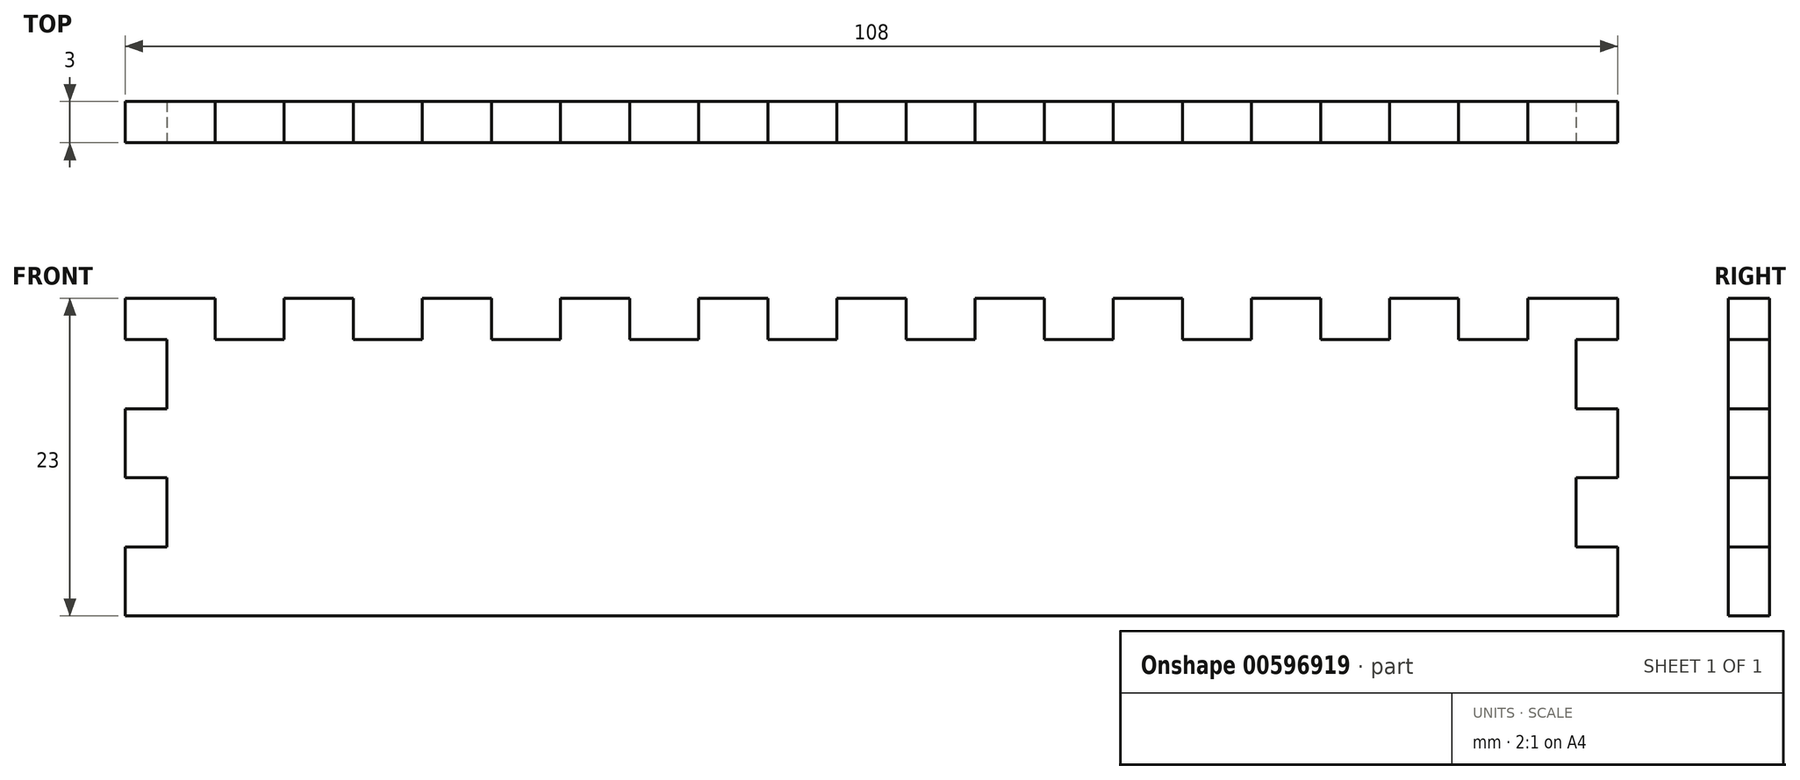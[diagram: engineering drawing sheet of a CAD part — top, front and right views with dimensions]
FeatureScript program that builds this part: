
annotation { "Feature Type Name" : "Feature", "Feature Type Description" : "" }
export const myFeature = defineFeature(function(context is Context, id is Id, definition is map)
    precondition{}
    {
        {
            var Q0;
            Q0=qCreatedBy(makeId("Front.planeOp"),FACE);
            var sketch = newSketch(context, id + "F0", { "sketchPlane" : qUnion([Q0])});
            skLineSegment(sketch, "E0.bottom", {"start": v(51, 20) * mm, "end": v(-51, 20) * mm});
            skLineSegment(sketch, "E0.top", {"start": v(51, -20) * mm, "end": v(-51, -20) * mm});
            skLineSegment(sketch, "E0.left", {"start": v(51, 20) * mm, "end": v(51, -20) * mm});
            skLineSegment(sketch, "E0.right", {"start": v(-51, 20) * mm, "end": v(-51, -20) * mm});
            skPoint(sketch, "E0.middle", {"position": v(0, 0) * mm});
            skSolve(sketch);
        }
        {
            var Q0;
            Q0=qSketchRegion(id+"F0",true);
            extrude(context, id + "F1", {"entities" : qUnion([Q0]), "depth" : 3 * mm, "offsetDistance" : 25 * mm});
        }
        {
            var Q0;
            Q0=makeQuery(id+"F1.opExtrude","CAP_FACE",FACE,{"disambiguationData":[OSD([sQuery(id+"F0.wireOp",EDGE,"E0.bottom"),sQuery(id+"F0.wireOp",EDGE,"E0.top"),sQuery(id+"F0.wireOp",EDGE,"E0.left"),sQuery(id+"F0.wireOp",EDGE,"E0.right")])],"isStart":false});
            var sketch = newSketch(context, id + "F2", { "sketchPlane" : qUnion([Q0])});
            skLineSegment(sketch, "E1.bottom", {"start": v(-51, -20) * mm, "end": v(-54, -20) * mm});
            skLineSegment(sketch, "E1.top", {"start": v(-51, -15) * mm, "end": v(-54, -15) * mm});
            skLineSegment(sketch, "E1.left", {"start": v(-51, -20) * mm, "end": v(-51, -15) * mm});
            skLineSegment(sketch, "E1.right", {"start": v(-54, -20) * mm, "end": v(-54, -15) * mm});
            skLineSegment(sketch, "E2.0.1.0", {"start": v(-51, -5) * mm, "end": v(-54, -5) * mm});
            skLineSegment(sketch, "E2.0.1.1", {"start": v(-54, -10) * mm, "end": v(-54, -5) * mm});
            skLineSegment(sketch, "E2.0.1.2", {"start": v(-51, -10) * mm, "end": v(-51, -5) * mm});
            skLineSegment(sketch, "E2.0.1.3", {"start": v(-51, -10) * mm, "end": v(-54, -10) * mm});
            skLineSegment(sketch, "E2.0.2.0", {"start": v(-51, 5) * mm, "end": v(-54, 5) * mm});
            skLineSegment(sketch, "E2.0.2.1", {"start": v(-54, 0) * mm, "end": v(-54, 5) * mm});
            skLineSegment(sketch, "E2.0.2.2", {"start": v(-51, 0) * mm, "end": v(-51, 5) * mm});
            skLineSegment(sketch, "E2.0.2.3", {"start": v(-51, 0) * mm, "end": v(-54, 0) * mm});
            skLineSegment(sketch, "E2.0.3.0", {"start": v(-51, 15) * mm, "end": v(-54, 15) * mm});
            skLineSegment(sketch, "E2.0.3.1", {"start": v(-54, 10) * mm, "end": v(-54, 15) * mm});
            skLineSegment(sketch, "E2.0.3.2", {"start": v(-51, 10) * mm, "end": v(-51, 15) * mm});
            skLineSegment(sketch, "E2.0.3.3", {"start": v(-51, 10) * mm, "end": v(-54, 10) * mm});
            skLineSegment(sketch, "E2.direction1", {"start": v(-54, -15) * mm, "end": v(-29, -15) * mm, "construction": true});
            skLineSegment(sketch, "E2.direction2", {"start": v(-54, -15) * mm, "end": v(-54, -5) * mm, "construction": true});
            skLineSegment(sketch, "E3.MirrorCS", {"start": v(54, -10) * mm, "end": v(54, -5) * mm});
            skLineSegment(sketch, "E4.MirrorCS", {"start": v(51, -5) * mm, "end": v(54, -5) * mm});
            skLineSegment(sketch, "E5.MirrorCS", {"start": v(51, -20) * mm, "end": v(51, -15) * mm});
            skLineSegment(sketch, "E6.MirrorCS", {"start": v(54, 10) * mm, "end": v(54, 15) * mm});
            skLineSegment(sketch, "E7.MirrorCS", {"start": v(51, -20) * mm, "end": v(54, -20) * mm});
            skLineSegment(sketch, "E8.MirrorCS", {"start": v(51, -15) * mm, "end": v(54, -15) * mm});
            skLineSegment(sketch, "E9.MirrorCS", {"start": v(54, -20) * mm, "end": v(54, -15) * mm});
            skLineSegment(sketch, "E10.MirrorCS", {"start": v(51, 15) * mm, "end": v(54, 15) * mm});
            skLineSegment(sketch, "E11.MirrorCS", {"start": v(51, 10) * mm, "end": v(54, 10) * mm});
            skLineSegment(sketch, "E12.MirrorCS", {"start": v(54, -15) * mm, "end": v(54, -5) * mm, "construction": true});
            skLineSegment(sketch, "E13.MirrorCS", {"start": v(51, 10) * mm, "end": v(51, 15) * mm});
            skLineSegment(sketch, "E14.MirrorCS", {"start": v(54, 0) * mm, "end": v(54, 5) * mm});
            skLineSegment(sketch, "E15.MirrorCS", {"start": v(51, 0) * mm, "end": v(51, 5) * mm});
            skLineSegment(sketch, "E16.MirrorCS", {"start": v(51, 0) * mm, "end": v(54, 0) * mm});
            skLineSegment(sketch, "E17.MirrorCS", {"start": v(51, -10) * mm, "end": v(51, -5) * mm});
            skLineSegment(sketch, "E18.MirrorCS", {"start": v(51, -10) * mm, "end": v(54, -10) * mm});
            skLineSegment(sketch, "E19.MirrorCS", {"start": v(51, 5) * mm, "end": v(54, 5) * mm});
            skSolve(sketch);
        }
        {
            var Q0;
            Q0=qSketchRegion(id+"F2",true);
            extrude(context, id + "F3", {"entities" : qUnion([Q0]), "operationType" : NewBodyOperationType.ADD, "oppositeDirection" : true, "depth" : 3 * mm, "offsetDistance" : 25 * mm});
        }
        {
            var Q0;
            Q0=makeQuery(id+"F3.boolean.opBoolean","MERGE",FACE,{"derivedFrom":[makeQuery(id+"F1.opExtrude","CAP_FACE",FACE,{"disambiguationData":[OSD([sQuery(id+"F0.wireOp",EDGE,"E0.bottom"),sQuery(id+"F0.wireOp",EDGE,"E0.top"),sQuery(id+"F0.wireOp",EDGE,"E0.left"),sQuery(id+"F0.wireOp",EDGE,"E0.right")])],"isStart":true}),makeQuery(id+"F3.opExtrude","CAP_FACE",FACE,{"disambiguationData":[OSD([sQuery(id+"F2.wireOp",EDGE,"E1.bottom"),sQuery(id+"F2.wireOp",EDGE,"E1.top"),sQuery(id+"F2.wireOp",EDGE,"E1.left"),sQuery(id+"F2.wireOp",EDGE,"E1.right")])],"isStart":false}),makeQuery(id+"F3.opExtrude","CAP_FACE",FACE,{"disambiguationData":[OSD([sQuery(id+"F2.wireOp",EDGE,"E2.0.1.0"),sQuery(id+"F2.wireOp",EDGE,"E2.0.1.1"),sQuery(id+"F2.wireOp",EDGE,"E2.0.1.2"),sQuery(id+"F2.wireOp",EDGE,"E2.0.1.3")])],"isStart":false}),makeQuery(id+"F3.opExtrude","CAP_FACE",FACE,{"disambiguationData":[OSD([sQuery(id+"F2.wireOp",EDGE,"E2.0.2.0"),sQuery(id+"F2.wireOp",EDGE,"E2.0.2.1"),sQuery(id+"F2.wireOp",EDGE,"E2.0.2.2"),sQuery(id+"F2.wireOp",EDGE,"E2.0.2.3")])],"isStart":false}),makeQuery(id+"F3.opExtrude","CAP_FACE",FACE,{"disambiguationData":[OSD([sQuery(id+"F2.wireOp",EDGE,"E2.0.3.0"),sQuery(id+"F2.wireOp",EDGE,"E2.0.3.1"),sQuery(id+"F2.wireOp",EDGE,"E2.0.3.2"),sQuery(id+"F2.wireOp",EDGE,"E2.0.3.3")])],"isStart":false}),makeQuery(id+"F3.opExtrude","CAP_FACE",FACE,{"disambiguationData":[OSD([sQuery(id+"F2.wireOp",EDGE,"E3.MirrorCS"),sQuery(id+"F2.wireOp",EDGE,"E4.MirrorCS"),sQuery(id+"F2.wireOp",EDGE,"E17.MirrorCS"),sQuery(id+"F2.wireOp",EDGE,"E18.MirrorCS")])],"isStart":false}),makeQuery(id+"F3.opExtrude","CAP_FACE",FACE,{"disambiguationData":[OSD([sQuery(id+"F2.wireOp",EDGE,"E5.MirrorCS"),sQuery(id+"F2.wireOp",EDGE,"E7.MirrorCS"),sQuery(id+"F2.wireOp",EDGE,"E8.MirrorCS"),sQuery(id+"F2.wireOp",EDGE,"E9.MirrorCS")])],"isStart":false}),makeQuery(id+"F3.opExtrude","CAP_FACE",FACE,{"disambiguationData":[OSD([sQuery(id+"F2.wireOp",EDGE,"E6.MirrorCS"),sQuery(id+"F2.wireOp",EDGE,"E10.MirrorCS"),sQuery(id+"F2.wireOp",EDGE,"E11.MirrorCS"),sQuery(id+"F2.wireOp",EDGE,"E13.MirrorCS")])],"isStart":false}),makeQuery(id+"F3.opExtrude","CAP_FACE",FACE,{"disambiguationData":[OSD([sQuery(id+"F2.wireOp",EDGE,"E14.MirrorCS"),sQuery(id+"F2.wireOp",EDGE,"E15.MirrorCS"),sQuery(id+"F2.wireOp",EDGE,"E16.MirrorCS"),sQuery(id+"F2.wireOp",EDGE,"E19.MirrorCS")])],"isStart":false})]});
            var sketch = newSketch(context, id + "F4", { "sketchPlane" : qUnion([Q0])});
            skLineSegment(sketch, "E20", {"start": v(0, 20) * mm, "end": v(0, 21.5) * mm, "construction": true});
            skLineSegment(sketch, "E21.bottom", {"start": v(-2.5, 20) * mm, "end": v(2.5, 20) * mm});
            skLineSegment(sketch, "E21.top", {"start": v(-2.5, 23) * mm, "end": v(2.5, 23) * mm});
            skLineSegment(sketch, "E21.left", {"start": v(-2.5, 20) * mm, "end": v(-2.5, 23) * mm});
            skLineSegment(sketch, "E21.right", {"start": v(2.5, 20) * mm, "end": v(2.5, 23) * mm});
            skPoint(sketch, "E21.middle", {"position": v(0, 21.5) * mm});
            skLineSegment(sketch, "E22.1.0.0", {"start": v(7.5, 23) * mm, "end": v(12.5, 23) * mm});
            skLineSegment(sketch, "E22.1.0.1", {"start": v(12.5, 20) * mm, "end": v(12.5, 23) * mm});
            skLineSegment(sketch, "E22.1.0.2", {"start": v(7.5, 20) * mm, "end": v(12.5, 20) * mm});
            skLineSegment(sketch, "E22.1.0.3", {"start": v(7.5, 20) * mm, "end": v(7.5, 23) * mm});
            skLineSegment(sketch, "E22.2.0.0", {"start": v(17.5, 23) * mm, "end": v(22.5, 23) * mm});
            skLineSegment(sketch, "E22.2.0.1", {"start": v(22.5, 20) * mm, "end": v(22.5, 23) * mm});
            skLineSegment(sketch, "E22.2.0.2", {"start": v(17.5, 20) * mm, "end": v(22.5, 20) * mm});
            skLineSegment(sketch, "E22.2.0.3", {"start": v(17.5, 20) * mm, "end": v(17.5, 23) * mm});
            skLineSegment(sketch, "E22.3.0.0", {"start": v(27.5, 23) * mm, "end": v(32.5, 23) * mm});
            skLineSegment(sketch, "E22.3.0.1", {"start": v(32.5, 20) * mm, "end": v(32.5, 23) * mm});
            skLineSegment(sketch, "E22.3.0.2", {"start": v(27.5, 20) * mm, "end": v(32.5, 20) * mm});
            skLineSegment(sketch, "E22.3.0.3", {"start": v(27.5, 20) * mm, "end": v(27.5, 23) * mm});
            skLineSegment(sketch, "E22.4.0.0", {"start": v(37.5, 23) * mm, "end": v(42.5, 23) * mm});
            skLineSegment(sketch, "E22.4.0.1", {"start": v(42.5, 20) * mm, "end": v(42.5, 23) * mm});
            skLineSegment(sketch, "E22.4.0.2", {"start": v(37.5, 20) * mm, "end": v(42.5, 20) * mm});
            skLineSegment(sketch, "E22.4.0.3", {"start": v(37.5, 20) * mm, "end": v(37.5, 23) * mm});
            skLineSegment(sketch, "E22.5.0.0", {"start": v(47.5, 23) * mm, "end": v(52.5, 23) * mm});
            skLineSegment(sketch, "E22.5.0.2", {"start": v(47.5, 20) * mm, "end": v(52.5, 20) * mm});
            skLineSegment(sketch, "E22.5.0.3", {"start": v(47.5, 20) * mm, "end": v(47.5, 23) * mm});
            skLineSegment(sketch, "E22.direction1", {"start": v(-2.5, 23) * mm, "end": v(7.5, 23) * mm, "construction": true});
            skLineSegment(sketch, "E23.MirrorCS", {"start": v(-47.5, 20) * mm, "end": v(-47.5, 23) * mm});
            skLineSegment(sketch, "E24.MirrorCS", {"start": v(-17.5, 20) * mm, "end": v(-17.5, 23) * mm});
            skLineSegment(sketch, "E25.MirrorCS", {"start": v(-22.5, 20) * mm, "end": v(-22.5, 23) * mm});
            skLineSegment(sketch, "E26.MirrorCS", {"start": v(-7.5, 20) * mm, "end": v(-7.5, 23) * mm});
            skLineSegment(sketch, "E27.MirrorCS", {"start": v(-12.5, 20) * mm, "end": v(-12.5, 23) * mm});
            skLineSegment(sketch, "E28.MirrorCS", {"start": v(-32.5, 20) * mm, "end": v(-32.5, 23) * mm});
            skLineSegment(sketch, "E29.MirrorCS", {"start": v(-37.5, 20) * mm, "end": v(-37.5, 23) * mm});
            skLineSegment(sketch, "E30.MirrorCS", {"start": v(-27.5, 20) * mm, "end": v(-27.5, 23) * mm});
            skLineSegment(sketch, "E31.MirrorCS", {"start": v(-42.5, 20) * mm, "end": v(-42.5, 23) * mm});
            skLineSegment(sketch, "E32.MirrorCS", {"start": v(-37.5, 23) * mm, "end": v(-42.5, 23) * mm});
            skLineSegment(sketch, "E33.MirrorCS", {"start": v(-47.5, 23) * mm, "end": v(-52.5, 23) * mm});
            skLineSegment(sketch, "E34.MirrorCS", {"start": v(-17.5, 20) * mm, "end": v(-22.5, 20) * mm});
            skLineSegment(sketch, "E35.MirrorCS", {"start": v(-17.5, 23) * mm, "end": v(-22.5, 23) * mm});
            skLineSegment(sketch, "E36.MirrorCS", {"start": v(-7.5, 20) * mm, "end": v(-12.5, 20) * mm});
            skLineSegment(sketch, "E37.MirrorCS", {"start": v(-7.5, 23) * mm, "end": v(-12.5, 23) * mm});
            skLineSegment(sketch, "E38.MirrorCS", {"start": v(-47.5, 20) * mm, "end": v(-52.5, 20) * mm});
            skLineSegment(sketch, "E39.MirrorCS", {"start": v(-27.5, 20) * mm, "end": v(-32.5, 20) * mm});
            skLineSegment(sketch, "E40.MirrorCS", {"start": v(-27.5, 23) * mm, "end": v(-32.5, 23) * mm});
            skLineSegment(sketch, "E41.MirrorCS", {"start": v(-37.5, 20) * mm, "end": v(-42.5, 20) * mm});
            skLineSegment(sketch, "E42", {"start": v(-52.5, 20) * mm, "end": v(-54, 20) * mm});
            skLineSegment(sketch, "E43", {"start": v(-54, 20) * mm, "end": v(-54, 23) * mm});
            skLineSegment(sketch, "E44", {"start": v(-54, 23) * mm, "end": v(-52.5, 23) * mm});
            skLineSegment(sketch, "E45.bottom", {"start": v(52.5, 23) * mm, "end": v(54, 23) * mm});
            skLineSegment(sketch, "E45.top", {"start": v(52.5, 20) * mm, "end": v(54, 20) * mm});
            skLineSegment(sketch, "E45.right", {"start": v(54, 23) * mm, "end": v(54, 20) * mm});
            skSolve(sketch);
        }
        {
            var Q0;
            Q0=qSketchRegion(id+"F4",true);
            extrude(context, id + "F5", {"entities" : qUnion([Q0]), "operationType" : NewBodyOperationType.ADD, "oppositeDirection" : true, "depth" : 3 * mm, "offsetDistance" : 25 * mm});
        }
        {
            var Q0;
            Q0=makeQuery(id+"F5.boolean.opBoolean","MERGE",FACE,{"derivedFrom":[makeQuery(id+"F3.boolean.opBoolean","MERGE",FACE,{"derivedFrom":[makeQuery(id+"F1.opExtrude","CAP_FACE",FACE,{"disambiguationData":[OSD([sQuery(id+"F0.wireOp",EDGE,"E0.bottom"),sQuery(id+"F0.wireOp",EDGE,"E0.top"),sQuery(id+"F0.wireOp",EDGE,"E0.left"),sQuery(id+"F0.wireOp",EDGE,"E0.right")])],"isStart":true}),makeQuery(id+"F3.opExtrude","CAP_FACE",FACE,{"disambiguationData":[OSD([sQuery(id+"F2.wireOp",EDGE,"E1.bottom"),sQuery(id+"F2.wireOp",EDGE,"E1.top"),sQuery(id+"F2.wireOp",EDGE,"E1.left"),sQuery(id+"F2.wireOp",EDGE,"E1.right")])],"isStart":false}),makeQuery(id+"F3.opExtrude","CAP_FACE",FACE,{"disambiguationData":[OSD([sQuery(id+"F2.wireOp",EDGE,"E2.0.1.0"),sQuery(id+"F2.wireOp",EDGE,"E2.0.1.1"),sQuery(id+"F2.wireOp",EDGE,"E2.0.1.2"),sQuery(id+"F2.wireOp",EDGE,"E2.0.1.3")])],"isStart":false}),makeQuery(id+"F3.opExtrude","CAP_FACE",FACE,{"disambiguationData":[OSD([sQuery(id+"F2.wireOp",EDGE,"E2.0.2.0"),sQuery(id+"F2.wireOp",EDGE,"E2.0.2.1"),sQuery(id+"F2.wireOp",EDGE,"E2.0.2.2"),sQuery(id+"F2.wireOp",EDGE,"E2.0.2.3")])],"isStart":false}),makeQuery(id+"F3.opExtrude","CAP_FACE",FACE,{"disambiguationData":[OSD([sQuery(id+"F2.wireOp",EDGE,"E2.0.3.0"),sQuery(id+"F2.wireOp",EDGE,"E2.0.3.1"),sQuery(id+"F2.wireOp",EDGE,"E2.0.3.2"),sQuery(id+"F2.wireOp",EDGE,"E2.0.3.3")])],"isStart":false}),makeQuery(id+"F3.opExtrude","CAP_FACE",FACE,{"disambiguationData":[OSD([sQuery(id+"F2.wireOp",EDGE,"E3.MirrorCS"),sQuery(id+"F2.wireOp",EDGE,"E4.MirrorCS"),sQuery(id+"F2.wireOp",EDGE,"E17.MirrorCS"),sQuery(id+"F2.wireOp",EDGE,"E18.MirrorCS")])],"isStart":false}),makeQuery(id+"F3.opExtrude","CAP_FACE",FACE,{"disambiguationData":[OSD([sQuery(id+"F2.wireOp",EDGE,"E5.MirrorCS"),sQuery(id+"F2.wireOp",EDGE,"E7.MirrorCS"),sQuery(id+"F2.wireOp",EDGE,"E8.MirrorCS"),sQuery(id+"F2.wireOp",EDGE,"E9.MirrorCS")])],"isStart":false}),makeQuery(id+"F3.opExtrude","CAP_FACE",FACE,{"disambiguationData":[OSD([sQuery(id+"F2.wireOp",EDGE,"E6.MirrorCS"),sQuery(id+"F2.wireOp",EDGE,"E10.MirrorCS"),sQuery(id+"F2.wireOp",EDGE,"E11.MirrorCS"),sQuery(id+"F2.wireOp",EDGE,"E13.MirrorCS")])],"isStart":false}),makeQuery(id+"F3.opExtrude","CAP_FACE",FACE,{"disambiguationData":[OSD([sQuery(id+"F2.wireOp",EDGE,"E14.MirrorCS"),sQuery(id+"F2.wireOp",EDGE,"E15.MirrorCS"),sQuery(id+"F2.wireOp",EDGE,"E16.MirrorCS"),sQuery(id+"F2.wireOp",EDGE,"E19.MirrorCS")])],"isStart":false})]}),makeQuery(id+"F5.opExtrude","CAP_FACE",FACE,{"disambiguationData":[OSD([sQuery(id+"F4.wireOp",EDGE,"E21.bottom"),sQuery(id+"F4.wireOp",EDGE,"E21.top"),sQuery(id+"F4.wireOp",EDGE,"E21.left"),sQuery(id+"F4.wireOp",EDGE,"E21.right")])],"isStart":true}),makeQuery(id+"F5.opExtrude","CAP_FACE",FACE,{"disambiguationData":[OSD([sQuery(id+"F4.wireOp",EDGE,"E22.1.0.0"),sQuery(id+"F4.wireOp",EDGE,"E22.1.0.1"),sQuery(id+"F4.wireOp",EDGE,"E22.1.0.2"),sQuery(id+"F4.wireOp",EDGE,"E22.1.0.3")])],"isStart":true}),makeQuery(id+"F5.opExtrude","CAP_FACE",FACE,{"disambiguationData":[OSD([sQuery(id+"F4.wireOp",EDGE,"E22.2.0.0"),sQuery(id+"F4.wireOp",EDGE,"E22.2.0.1"),sQuery(id+"F4.wireOp",EDGE,"E22.2.0.2"),sQuery(id+"F4.wireOp",EDGE,"E22.2.0.3")])],"isStart":true}),makeQuery(id+"F5.opExtrude","CAP_FACE",FACE,{"disambiguationData":[OSD([sQuery(id+"F4.wireOp",EDGE,"E22.3.0.0"),sQuery(id+"F4.wireOp",EDGE,"E22.3.0.1"),sQuery(id+"F4.wireOp",EDGE,"E22.3.0.2"),sQuery(id+"F4.wireOp",EDGE,"E22.3.0.3")])],"isStart":true}),makeQuery(id+"F5.opExtrude","CAP_FACE",FACE,{"disambiguationData":[OSD([sQuery(id+"F4.wireOp",EDGE,"E22.4.0.0"),sQuery(id+"F4.wireOp",EDGE,"E22.4.0.1"),sQuery(id+"F4.wireOp",EDGE,"E22.4.0.2"),sQuery(id+"F4.wireOp",EDGE,"E22.4.0.3")])],"isStart":true}),makeQuery(id+"F5.opExtrude","CAP_FACE",FACE,{"disambiguationData":[OSD([sQuery(id+"F4.wireOp",EDGE,"E22.5.0.0"),sQuery(id+"F4.wireOp",EDGE,"E22.5.0.2"),sQuery(id+"F4.wireOp",EDGE,"E22.5.0.3"),sQuery(id+"F4.wireOp",EDGE,"E45.bottom"),sQuery(id+"F4.wireOp",EDGE,"E45.top"),sQuery(id+"F4.wireOp",EDGE,"E45.right")])],"isStart":true}),makeQuery(id+"F5.opExtrude","CAP_FACE",FACE,{"disambiguationData":[OSD([sQuery(id+"F4.wireOp",EDGE,"E23.MirrorCS"),sQuery(id+"F4.wireOp",EDGE,"E33.MirrorCS"),sQuery(id+"F4.wireOp",EDGE,"E38.MirrorCS"),sQuery(id+"F4.wireOp",EDGE,"E42"),sQuery(id+"F4.wireOp",EDGE,"E43"),sQuery(id+"F4.wireOp",EDGE,"E44")])],"isStart":true}),makeQuery(id+"F5.opExtrude","CAP_FACE",FACE,{"disambiguationData":[OSD([sQuery(id+"F4.wireOp",EDGE,"E24.MirrorCS"),sQuery(id+"F4.wireOp",EDGE,"E25.MirrorCS"),sQuery(id+"F4.wireOp",EDGE,"E34.MirrorCS"),sQuery(id+"F4.wireOp",EDGE,"E35.MirrorCS")])],"isStart":true}),makeQuery(id+"F5.opExtrude","CAP_FACE",FACE,{"disambiguationData":[OSD([sQuery(id+"F4.wireOp",EDGE,"E26.MirrorCS"),sQuery(id+"F4.wireOp",EDGE,"E27.MirrorCS"),sQuery(id+"F4.wireOp",EDGE,"E36.MirrorCS"),sQuery(id+"F4.wireOp",EDGE,"E37.MirrorCS")])],"isStart":true}),makeQuery(id+"F5.opExtrude","CAP_FACE",FACE,{"disambiguationData":[OSD([sQuery(id+"F4.wireOp",EDGE,"E28.MirrorCS"),sQuery(id+"F4.wireOp",EDGE,"E30.MirrorCS"),sQuery(id+"F4.wireOp",EDGE,"E39.MirrorCS"),sQuery(id+"F4.wireOp",EDGE,"E40.MirrorCS")])],"isStart":true}),makeQuery(id+"F5.opExtrude","CAP_FACE",FACE,{"disambiguationData":[OSD([sQuery(id+"F4.wireOp",EDGE,"E29.MirrorCS"),sQuery(id+"F4.wireOp",EDGE,"E31.MirrorCS"),sQuery(id+"F4.wireOp",EDGE,"E32.MirrorCS"),sQuery(id+"F4.wireOp",EDGE,"E41.MirrorCS")])],"isStart":true})]});
            var sketch = newSketch(context, id + "F6", { "sketchPlane" : qUnion([Q0])});
            skLineSegment(sketch, "E46.bottom", {"start": v(-54, -20) * mm, "end": v(54, -20) * mm});
            skLineSegment(sketch, "E46.top", {"start": v(-54, 0) * mm, "end": v(54, 0) * mm});
            skLineSegment(sketch, "E46.left", {"start": v(-54, -20) * mm, "end": v(-54, 0) * mm});
            skLineSegment(sketch, "E46.right", {"start": v(54, -20) * mm, "end": v(54, 0) * mm});
            skSolve(sketch);
        }
        {
            var Q0;
            Q0 = qSketchRegion(id + "F6", true);
            extrude(context, id + "F7", {"entities" : qUnion([Q0]), "operationType" : NewBodyOperationType.REMOVE, "oppositeDirection" : true, "depth" : 25 * mm, "offsetDistance" : 25 * mm});
        }
    });
